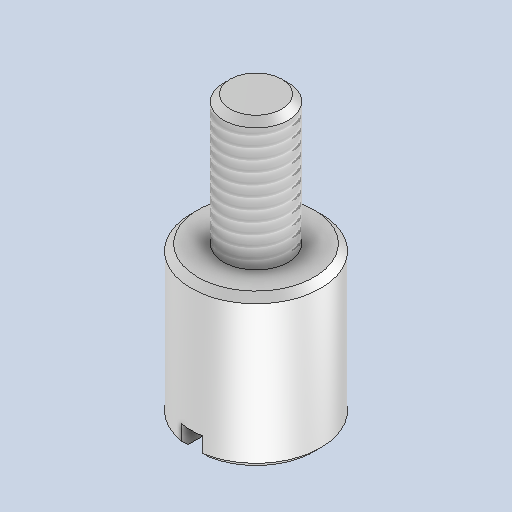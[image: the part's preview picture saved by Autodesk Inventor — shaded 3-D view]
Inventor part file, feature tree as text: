
AUTODESK INVENTOR PART (.ipt)
format: ipt  version: 2024.2 (Build 282272000, 272)  size: 318,976 bytes
history: native  units: mm
features: sketch x2, revolve x1, extrude x1, hole x1, thread x1, chamfer x1
ambient origin geometry x8: Origin, YZ Plane, XZ Plane, XY Plane, X Axis, Y Axis, Z Axis, Center Point
bodies: Solid1 (feature_tree)
feature tree (7):
  revolve  "Revolution1"  [1 undecoded]
  sketch  "Sketch2"  dims[d3=3.0mm d4=6.0mm d5=90.0deg d6=1.0mm d7=1.0mm d8=0.0mm d9=2.459mm d10=6.0mm d11=4.0mm d12=2.0mm d13=90.0deg d14=6.0mm d15=0.0mm d16=6.0mm d17=0.0mm d18=0.3mm d19=2.0mm d20=45.0deg]
  extrude  "Extrusion1"  Depth=3.0mm
  hole  "Hole1"  [1 undecoded]
  thread  "Thread1"  [1 undecoded]
  chamfer  "Chamfer1"  Distance=1.0mm
  sketch  "Sketch1"  dims[d1=6.0mm d2=7.0mm]
note: 3 required parameter values undecoded (feature->parameter linkage not recoverable at this tier; creation-order binding heuristic only, values carry confidence <= 0.55)